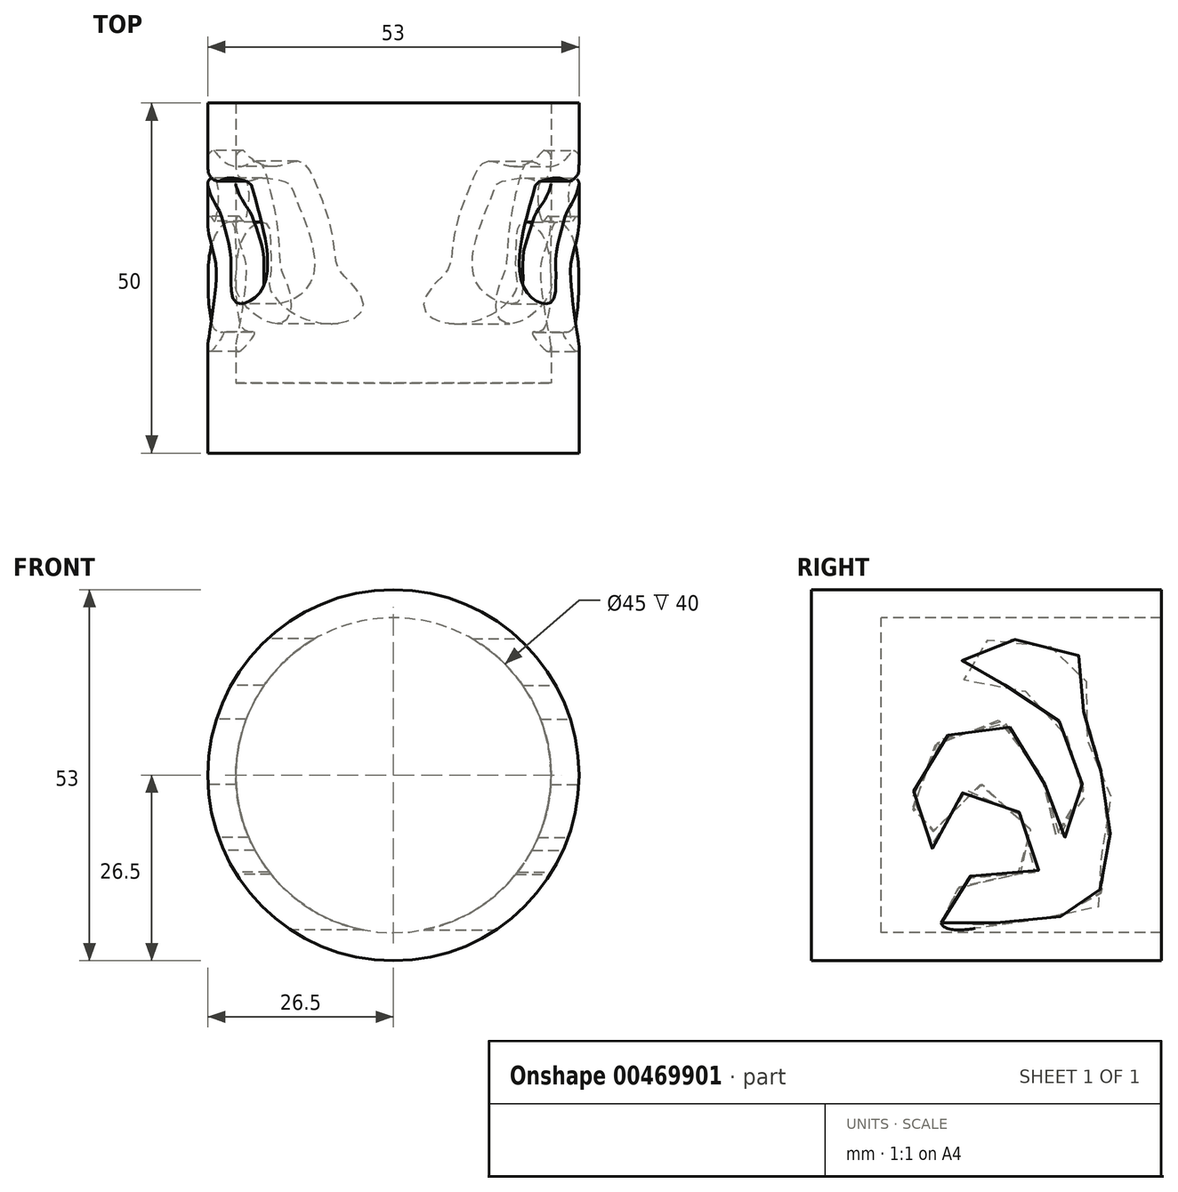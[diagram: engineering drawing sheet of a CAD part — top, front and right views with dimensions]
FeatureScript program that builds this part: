
annotation { "Feature Type Name" : "Feature", "Feature Type Description" : "" }
export const myFeature = defineFeature(function(context is Context, id is Id, definition is map)
    precondition{}
    {
        {
            var Q0;
            Q0=qCreatedBy(makeId("Front.planeOp"),FACE);
            var sketch = newSketch(context, id + "F0", { "sketchPlane" : qUnion([Q0])});
            skCircle(sketch, "E0", {"center": v(0, 0) * mm, "radius": 26.5 * mm});
            skSolve(sketch);
        }
        {
            var Q0;
            Q0=makeQuery(id+"F0.imprint","IMPRINT",FACE,{"disambiguationData":[TD([[makeQuery(id+"F0.imprint","IMPRINT",EDGE,{"derivedFrom":sQuery(id+"F0.wireOp",EDGE,"E0")}),1.0]])]});
            var Q1;
            Q1 = qSketchRegion(id + "F0", true);
            extrude(context, id + "F1", {"entities" : qUnion([Q0, Q1]), "depth" : 40 * mm});
        }
        {
            var Q0;
            Q0=makeQuery(id+"F1.opExtrude","CAP_FACE",FACE,{"disambiguationData":[OSD([sQuery(id+"F0.wireOp",EDGE,"E0")])],"isStart":false});
            var sketch = newSketch(context, id + "F2", { "sketchPlane" : qUnion([Q0])});
            skCircle(sketch, "E1", {"center": v(0, 0) * mm, "radius": 22.5 * mm});
            skSolve(sketch);
        }
        {
            var Q0;
            Q0 = qSketchRegion(id + "F2", true);
            extrude(context, id + "F3", {"entities" : qUnion([Q0]), "operationType" : NewBodyOperationType.REMOVE, "endBound" : BoundingType.THROUGH_ALL, "oppositeDirection" : true, "depth" : 25 * mm});
        }
        {
            var Q0;
            Q0=qCreatedBy(makeId("Right.planeOp"),FACE);
            var sketch = newSketch(context, id + "F4", { "sketchPlane" : qUnion([Q0])});
            skFitSpline(sketch, "E2", {"points": [v(-31.44, -21.09) * mm, v(-26.72, -14.06) * mm, v(-24.76, -14.06) * mm, v(-20.03, -14.06) * mm, v(-17.03, -12.79) * mm, v(-24.64, -1.49) * mm, v(-30.06, -4.02) * mm, v(-31.68, -5.64) * mm, v(-32.71, -9.33) * mm, v(-32.83, -10.71) * mm, v(-35.13, -6.56) * mm, v(-34.79, 0) * mm, v(-31.68, 4.85) * mm, v(-24.53, 7.97) * mm, v(-21.64, 6.81) * mm, v(-17.15, 0) * mm, v(-16.34, -5.3) * mm, v(-16.69, -7.6) * mm, v(-11.73, -8.52) * mm, v(-11.15, -2.06) * mm, v(-12.3, 2.9) * mm, v(-14.84, 8.2) * mm, v(-16.1, 9.93) * mm, v(-19.1, 11.77) * mm, v(-22.1, 12.8) * mm, v(-27.64, 13.16) * mm, v(-28.68, 15.23) * mm, v(-26.83, 18.57) * mm, v(-18.76, 19.04) * mm, v(-11.73, 17.08) * mm, v(-11.38, 16.85) * mm, v(-10.7, 12.35) * mm, v(-11.15, 8.77) * mm, v(-10.34, 3.82) * mm, v(-9.54, 1.28) * mm, v(-8.04, 0) * mm, v(-7.23, -2.99) * mm, v(-6.77, -6.56) * mm, v(-7.12, -7.83) * mm, v(-8.5, -11.29) * mm, v(-8.96, -15.67) * mm, v(-8.38, -18.2) * mm, v(-11.5, -19.59) * mm, v(-18.65, -20.74) * mm, v(-23.72, -21.09) * mm, v(-26.14, -21.78) * mm, v(-31.44, -21.09) * mm]});
            skSolve(sketch);
        }
        {
            var Q0;
            Q0 = qSketchRegion(id + "F4", true);
            extrude(context, id + "F5", {"entities" : qUnion([Q0]), "operationType" : NewBodyOperationType.REMOVE, "endBound" : BoundingType.THROUGH_ALL, "oppositeDirection" : true, "depth" : 25 * mm, "hasSecondDirection" : true, "secondDirectionBound" : SecondDirectionBoundingType.THROUGH_ALL, "secondDirectionOppositeDirection" : false, "secondDirectionDepth" : 25 * mm});
        }
        {
            var Q0;
            Q0=makeQuery(id+"F1.opExtrude","CAP_FACE",FACE,{"disambiguationData":[OSD([sQuery(id+"F0.wireOp",EDGE,"E0")])],"isStart":false});
            var sketch = newSketch(context, id + "F6", { "sketchPlane" : qUnion([Q0])});
            skSolve(sketch);
        }
        {
            var Q0;
            Q0=makeQuery(id+"F6.imprint","IMPRINT",FACE,{"disambiguationData":[TD([[makeQuery(id+"F6.imprint","IMPRINT",EDGE,{"derivedFrom":makeQuery(id+"F1.opExtrude","CAP_EDGE",EDGE,{"disambiguationData":[OSD([sQuery(id+"F0.wireOp",EDGE,"E0")])],"isStart":false})}),1.0]])]});
            var sketch = newSketch(context, id + "F7", { "sketchPlane" : qUnion([Q0])});
            skCircle(sketch, "E3", {"center": v(0, 0) * mm, "radius": 26.5 * mm});
            skSolve(sketch);
        }
        {
            var Q0;
            Q0 = qSketchRegion(id + "F7", true);
            extrude(context, id + "F8", {"entities" : qUnion([Q0]), "operationType" : NewBodyOperationType.ADD, "depth" : 10 * mm});
        }
    });
